# Revit family: Zumtobel CLEAN II
name_source: partatom
category: Lighting Fixtures
revit_build: Autodesk Revit 2018 (Build: 20170223_1515(x64)
units: mm (PartAtom-declared; Revit-internal decimal feet)

## family parameters
Cut with Voids When Loaded = No
Host = Face
Light Source = Yes
OmniClass Number = 23.80.70.11
OmniClass Title = Luminaries for Internal Lighting
Part Type = Normal
Room Calculation Point = No
Round Connector Dimension = Use Diameter
Shared = No

## types (1)
- CL2 S 6600-840 M600Q SG MP LDO
    Apparent Load = 40 VA
    Assembly Code = D5020200
    Body = ZGl_Metal_Aluminium
    Color Filter = 16777215
    Cover = ZG_PMMA_Self_llumination_Opaque
    Default Elevation = 0 mm  [stored 0 ft]
    Description = Surface mount luminaire
    Dimming Lamp Color Temperature Shift = <None>
    Emit Shape Visible in Rendering = Yes
    Emit from Rectangle Length = 578 mm  [stored 1.89633 ft]
    Emit from Rectangle Width = 578 mm  [stored 1.89633 ft]
    Height = 105 mm  [stored 0.344488 ft]
    Lamp = LED
    Length = 598 mm  [stored 1.96194 ft]
    Manufacturer = Zumtobel Lighting
    Model = 42186912
    Offset = 100 mm  [stored 0.328084 ft]
    Photometric Web File = 42186912_(STD_LEO).IES
    Recessed = No
    Surface Mount = Yes
    Tilt Angle = 90.00°
    Top Offset = 105 mm  [stored 0.344488 ft]
    URL = http://www.zumtobel.com
    Voltage = 230 V
    Width = 598 mm  [stored 1.96194 ft]

note: [stored X ft] marks values corroborated as IEEE doubles in the binary element streams (Revit-internal decimal feet)

## geometry (parser evidence)
native form markers: Sweep x3
no freeform markers — native parametric forms only
